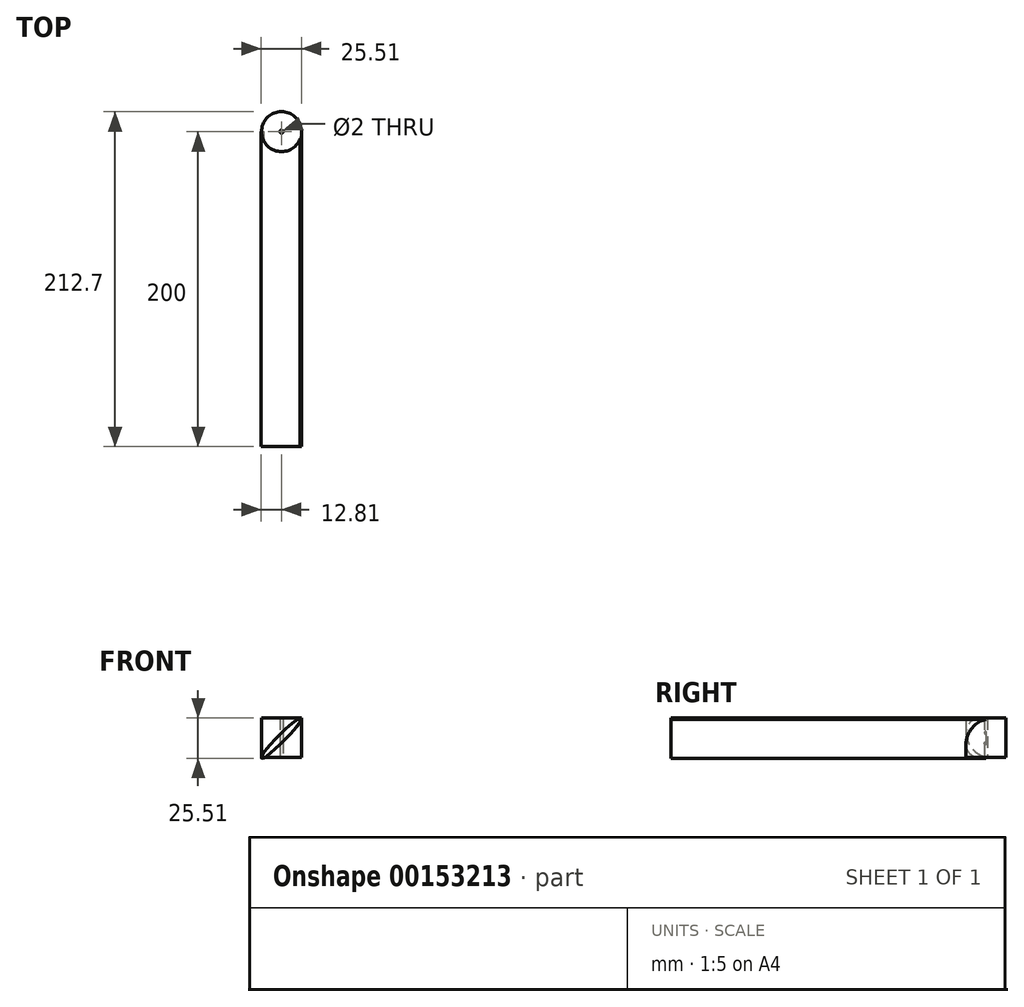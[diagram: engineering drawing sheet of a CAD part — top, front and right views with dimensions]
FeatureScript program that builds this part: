
annotation { "Feature Type Name" : "Feature", "Feature Type Description" : "" }
export const myFeature = defineFeature(function(context is Context, id is Id, definition is map)
    precondition{}
    {
        {
            var Q0;
            Q0=qCreatedBy(makeId("Top.planeOp"),FACE);
            var sketch = newSketch(context, id + "F0", { "sketchPlane" : qUnion([Q0])});
            skCircle(sketch, "E0", {"center": v(0, 0) * mm, "radius": 12.7 * mm});
            skCircle(sketch, "E1", {"center": v(0, 0) * mm, "radius": 1 * mm});
            skSolve(sketch);
        }
        {
            var Q0;
            Q0=makeQuery(id+"F0.imprint","IMPRINT",FACE,{"disambiguationData":[TD([[makeQuery(id+"F0.imprint","IMPRINT",EDGE,{"derivedFrom":sQuery(id+"F0.wireOp",EDGE,"E0")}),1.0]])]});
            extrude(context, id + "F1", {"entities" : qUnion([Q0]), "depth" : 25 * mm});
        }
        {
            var Q0;
            Q0=qCreatedBy(makeId("Front.planeOp"),FACE);
            var sketch = newSketch(context, id + "F2", { "sketchPlane" : qUnion([Q0])});
            skLineSegment(sketch, "E2.0", {"start": v(-12.7, 25) * mm, "end": v(12.7, 25) * mm});
            skLineSegment(sketch, "E3", {"start": v(-12.7, 0) * mm, "end": v(-12.7, 25) * mm});
            skLineSegment(sketch, "E4", {"start": v(-12.7, 0) * mm, "end": v(-12.7, 24.6) * mm});
            skLineSegment(sketch, "E5", {"start": v(12.7, 24.6) * mm, "end": v(12.7, 0) * mm});
            skLineSegment(sketch, "E6", {"start": v(12.7, 25) * mm, "end": v(12.7, 0) * mm});
            skLineSegment(sketch, "E7", {"start": v(12.7, 12.3) * mm, "end": v(-12.7, 12.3) * mm, "construction": true});
            skLineSegment(sketch, "E8", {"start": v(0, 0) * mm, "end": v(0, 25) * mm, "construction": true});
            skLineSegment(sketch, "E9", {"start": v(0, 12.3) * mm, "end": v(12.7, 25) * mm, "construction": true});
            skEllipse(sketch, "E10", {"center": v(0, 12.3) * mm, "majorRadius": 17.96 * mm, "minorRadius": 2.38 * mm, "majorAxis": v(0.7, 0.7)});
            skSolve(sketch);
        }
        {
            var Q0;
            {var subQ4=sQuery(id+"F2.wireOp",EDGE,"E6");var subQ5=makeQuery(id+"F2.imprint","IMPRINT",VERTEX,{"derivedFrom":subQ4});Q0=makeQuery(id+"F2.imprint","IMPRINT",FACE,{"disambiguationData":[TD([[makeQuery(id+"F2.imprint","IMPRINT",EDGE,{"disambiguationData":[TD([[subQ5,-1.0]])],"derivedFrom":subQ4}),-1.0]])]});}
            extrude(context, id + "F3", {"entities" : qUnion([Q0]), "operationType" : NewBodyOperationType.ADD, "depth" : 200 * mm});
        }
        {
            var Q0;
            Q0=sQuery(id+"F2.wireOp",EDGE,"E9");
            var Q1;
            Q1=sQuery(id+"F2.wireOp",EDGE,"E7");
            cPlane(context, id + "F4", {"entities" : qUnion([Q0, Q1]), "cplaneType" : CPlaneType.LINE_ANGLE, "offset" : 25 * mm, "angle" : 90 * degree, "width" : 150 * mm, "height" : 150 * mm});
        }
    });
